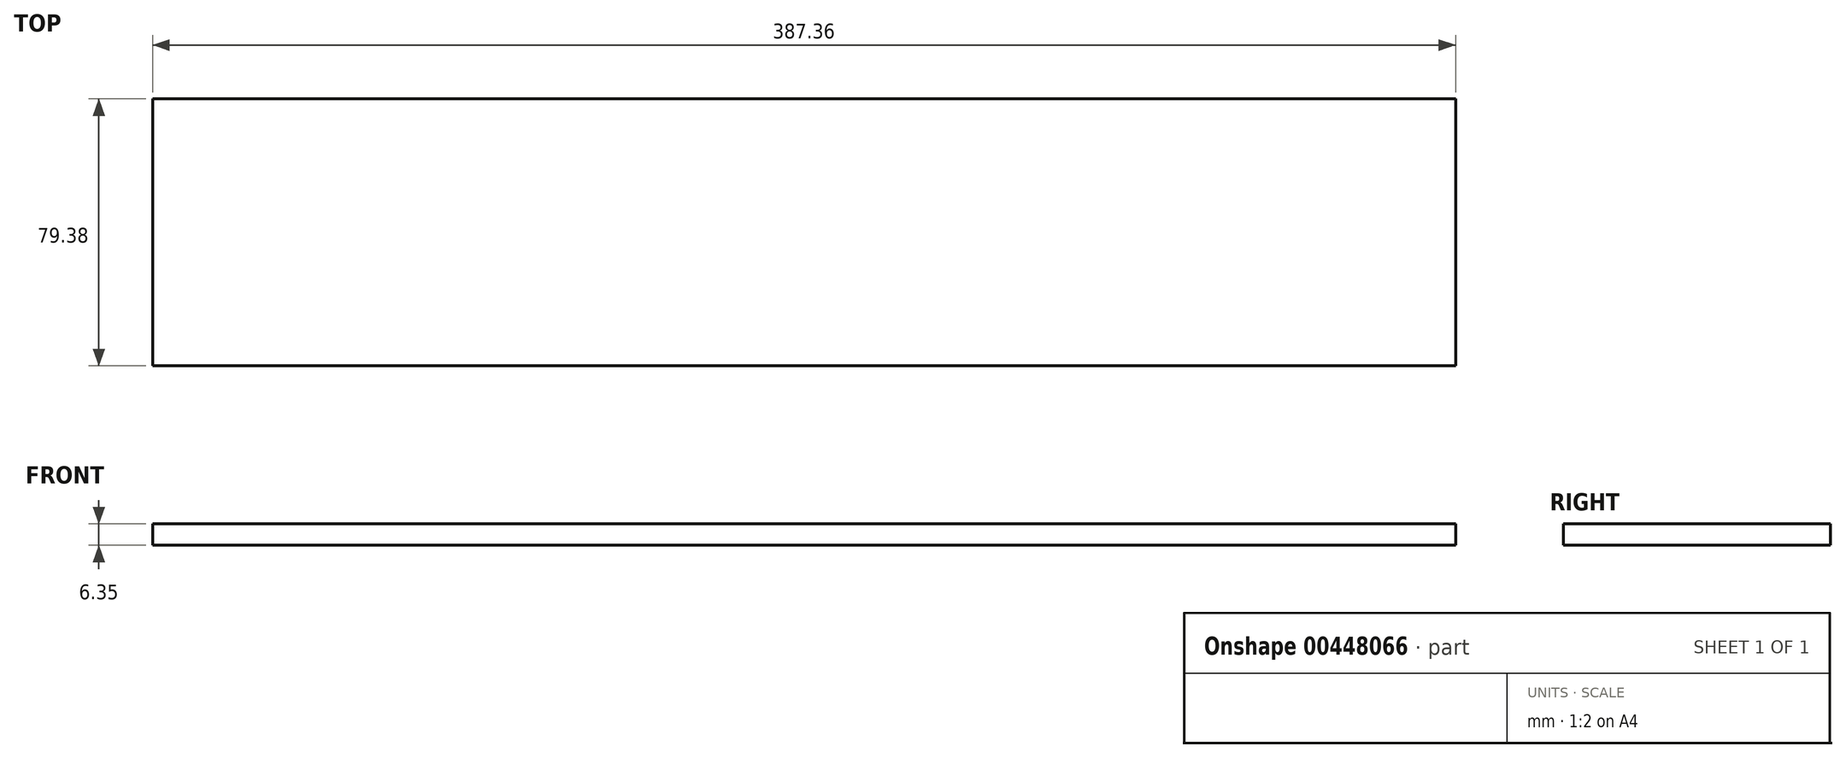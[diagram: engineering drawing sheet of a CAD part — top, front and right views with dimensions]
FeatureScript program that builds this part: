
annotation { "Feature Type Name" : "Feature", "Feature Type Description" : "" }
export const myFeature = defineFeature(function(context is Context, id is Id, definition is map)
    precondition{}
    {
        {
            var Q0;
            Q0=qCreatedBy(makeId("Top.planeOp"),FACE);
            var sketch = newSketch(context, id + "F0", { "sketchPlane" : qUnion([Q0])});
            skLineSegment(sketch, "E0.bottom", {"start": v(-193.67, 39.69) * mm, "end": v(193.67, 39.69) * mm});
            skLineSegment(sketch, "E0.top", {"start": v(-193.67, -39.69) * mm, "end": v(193.67, -39.69) * mm});
            skLineSegment(sketch, "E0.left", {"start": v(-193.67, 39.69) * mm, "end": v(-193.67, -39.69) * mm});
            skLineSegment(sketch, "E0.right", {"start": v(193.67, 39.69) * mm, "end": v(193.67, -39.69) * mm});
            skPoint(sketch, "E0.middle", {"position": v(0, 0) * mm});
            skSolve(sketch);
        }
        {
            var Q0;
            Q0=qSketchRegion(id+"F0",true);
            extrude(context, id + "F1", {"entities" : qUnion([Q0]), "depth" : 6.35 * mm});
        }
    });
